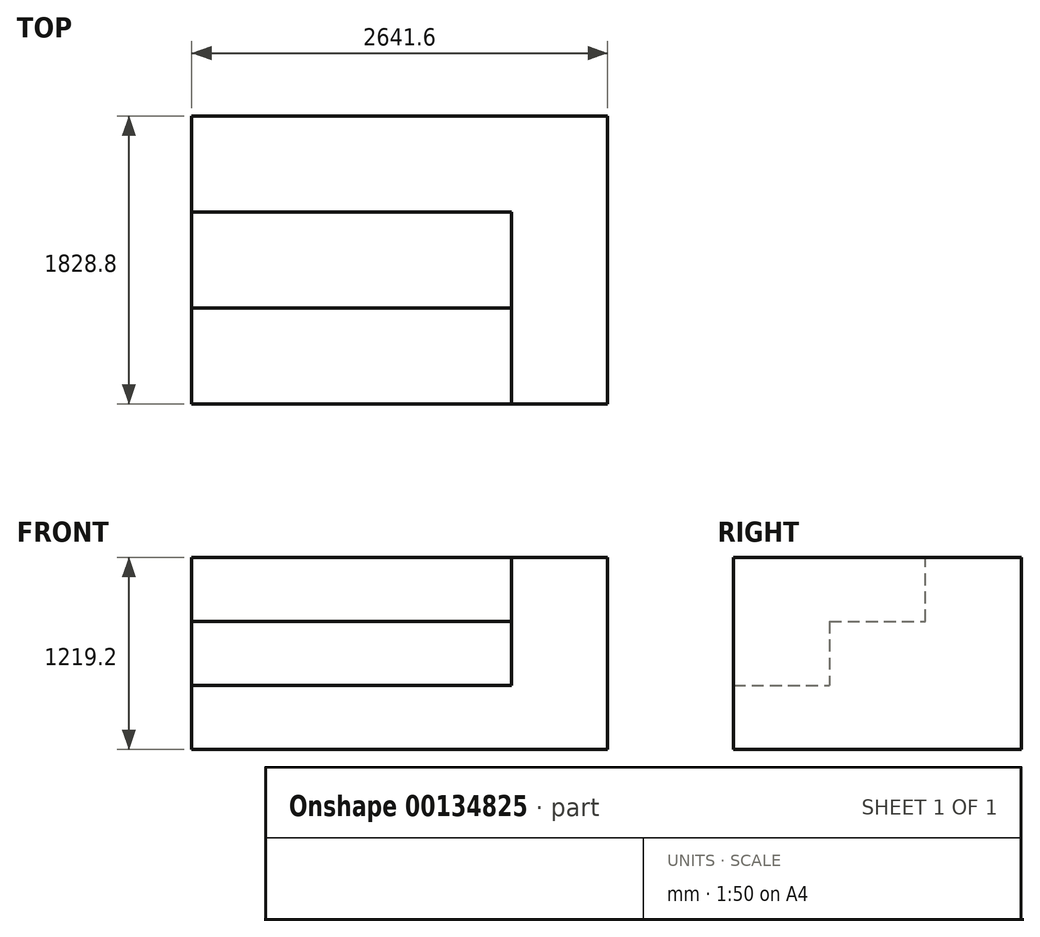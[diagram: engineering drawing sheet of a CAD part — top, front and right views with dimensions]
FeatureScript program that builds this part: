
annotation { "Feature Type Name" : "Feature", "Feature Type Description" : "" }
export const myFeature = defineFeature(function(context is Context, id is Id, definition is map)
    precondition{}
    {
        {
            var Q0;
            Q0=qCreatedBy(makeId("Top.planeOp"),FACE);
            var sketch = newSketch(context, id + "F0", { "sketchPlane" : qUnion([Q0])});
            skLineSegment(sketch, "E0.bottom", {"start": v(-1320.8, 914.4) * mm, "end": v(1320.8, 914.4) * mm});
            skLineSegment(sketch, "E0.top", {"start": v(-1320.8, -914.4) * mm, "end": v(1320.8, -914.4) * mm});
            skLineSegment(sketch, "E0.left", {"start": v(-1320.8, 914.4) * mm, "end": v(-1320.8, -914.4) * mm});
            skLineSegment(sketch, "E0.right", {"start": v(1320.8, 914.4) * mm, "end": v(1320.8, -914.4) * mm});
            skPoint(sketch, "E0.middle", {"position": v(0, 0) * mm});
            skSolve(sketch);
        }
        {
            var Q0;
            Q0=makeQuery(id+"F0.imprint","IMPRINT",FACE,{"disambiguationData":[TD([[makeQuery(id+"F0.imprint","IMPRINT",EDGE,{"derivedFrom":sQuery(id+"F0.wireOp",EDGE,"E0.bottom")}),-1.0]])]});
            extrude(context, id + "F1", {"entities" : qUnion([Q0]), "depth" : 1219.2 * mm});
        }
        {
            var Q0;
            Q0=makeQuery(id+"F1.opExtrude","CAP_FACE",FACE,{"disambiguationData":[OSD([sQuery(id+"F0.wireOp",EDGE,"E0.bottom"),sQuery(id+"F0.wireOp",EDGE,"E0.top"),sQuery(id+"F0.wireOp",EDGE,"E0.left"),sQuery(id+"F0.wireOp",EDGE,"E0.right")])],"isStart":false});
            var sketch = newSketch(context, id + "F2", { "sketchPlane" : qUnion([Q0])});
            skLineSegment(sketch, "E1.bottom", {"start": v(-1320.8, -914.4) * mm, "end": v(711.2, -914.4) * mm});
            skLineSegment(sketch, "E1.top", {"start": v(-1320.8, 304.8) * mm, "end": v(711.2, 304.8) * mm});
            skLineSegment(sketch, "E1.left", {"start": v(-1320.8, -914.4) * mm, "end": v(-1320.8, 304.8) * mm});
            skLineSegment(sketch, "E1.right", {"start": v(711.2, -914.4) * mm, "end": v(711.2, 304.8) * mm});
            skSolve(sketch);
        }
        {
            var Q0;
            Q0=makeQuery(id+"F2.imprint","IMPRINT",FACE,{"disambiguationData":[TD([[makeQuery(id+"F2.imprint","IMPRINT",EDGE,{"derivedFrom":sQuery(id+"F2.wireOp",EDGE,"E1.bottom")}),1.0]])]});
            extrude(context, id + "F3", {"entities" : qUnion([Q0]), "operationType" : NewBodyOperationType.REMOVE, "oppositeDirection" : true, "depth" : 812.8 * mm});
        }
        {
            var Q0;
            Q0=makeQuery(id+"F3.boolean.opBoolean","COPY",FACE,{"derivedFrom":makeQuery(id+"F3.opExtrude","CAP_FACE",FACE,{"disambiguationData":[OSD([sQuery(id+"F2.wireOp",EDGE,"E1.bottom"),sQuery(id+"F2.wireOp",EDGE,"E1.top"),sQuery(id+"F2.wireOp",EDGE,"E1.left"),sQuery(id+"F2.wireOp",EDGE,"E1.right")])],"isStart":false})});
            var sketch = newSketch(context, id + "F4", { "sketchPlane" : qUnion([Q0])});
            skLineSegment(sketch, "E2.bottom", {"start": v(-1320.8, 304.8) * mm, "end": v(711.2, 304.8) * mm});
            skLineSegment(sketch, "E2.top", {"start": v(-1320.8, -304.8) * mm, "end": v(711.2, -304.8) * mm});
            skLineSegment(sketch, "E2.left", {"start": v(-1320.8, 304.8) * mm, "end": v(-1320.8, -304.8) * mm});
            skLineSegment(sketch, "E2.right", {"start": v(711.2, 304.8) * mm, "end": v(711.2, -304.8) * mm});
            skSolve(sketch);
        }
        {
            var Q0;
            Q0=makeQuery(id+"F4.imprint","IMPRINT",FACE,{"disambiguationData":[TD([[makeQuery(id+"F4.imprint","IMPRINT",EDGE,{"derivedFrom":sQuery(id+"F4.wireOp",EDGE,"E2.bottom")}),-1.0]])]});
            extrude(context, id + "F5", {"entities" : qUnion([Q0]), "operationType" : NewBodyOperationType.ADD, "depth" : 406.4 * mm});
        }
    });
